# Revit family: Deca_Bacia Carrara_P.606_Caixa Acoplada
name_source: partatom
category: Plumbing Fixtures
revit_build: Autodesk Revit Architecture 2012 (Build: 20110916_2132(x64)
units: mm (PartAtom-declared; Revit-internal decimal feet)

## types (3) — shared parameters
Acompanha o Produto = Não Aplicável
Aprovado por = Contino/quattroD
Atendimento ao Cliente = 0800-011-7073
Consumo = 6 LPF
Criador por = Contino/quattroD
Description = Bacia com caixa acoplada
Descrição = Bacia com caixa acoplada
Diâmetro Ponto de Esgoto = 100 mm  [stored 0.328084 ft]
Fabricante = Deca
Linha = Carrara
Louça/Metais = Louça
Manufacturer = Deca
Material = Cerâmica (Vitreous China)
Norma = NBR15097-1 NBR15097-2
Peso Liquido (Kg) = 33.8
Produto = Bacia para caixa acoplada linha Carrara
Raio Ponto de Esgoto = 50 mm  [stored 0.164042 ft]
Segmento = Banheiro Luxo
URL = www.deca.com.br
Variações de COR = P.606.17, P.606.37 , P.606.95
Vendido Separadamente = Anel de vedação (AV.90.01 ), Ligação flexível (4607.C.030 / 4607.C.040 / 4607.C.050), Parafusos de fixação (SP.13.01)
zero-valued in all types: Default Elevation

## per-type parameters (varying)
| type | Assento | Bacia | Caixa | Caixa_Family | Código | Diâmetro Água Fria | Model | Raio Água Fria |
| Dual Flux 3 lpf / 6 lpf - Branco GE17 | Deca GE17 Branco Gelo Poliéster | Deca GE17 Branco Gelo Cerâmica | Deca GE17 Branco Gelo Cerâmica | Deca_Shared_Caixa Acoplada_P.606 : Dual Flux 3 lpf / 6 lpf - Branco GE17 | P.606.17 | 15 mm  [stored 0.0492126 ft] | P.606.17 | 8 mm  [stored 0.0262467 ft] |
| Dual Flux 3 lpf / 6 lpf - Ébano EB95 | Deca EB95 Ébano Poliéster | Deca EB95 Ébano Cerâmica | Deca EB95 Ébano Cerâmica | Deca_Shared_Caixa Acoplada_P.606 : Dual Flux 3 lpf / 6 lpf - Ébano EB95 | P.606.95 | 13 mm | P.606.95 | 6 mm  [stored 0.019685 ft] |
| Dual Flux 3 lpf / 6 lpf - Creme CR37 | Deca CR37 Creme Poliéster | Deca CR37 Creme Cerâmica | Deca CR37 Creme Cerâmica | Deca_Shared_Caixa Acoplada_P.606 : Dual Flux 3 lpf / 6 lpf - Creme CR37 | P.606.37 | 13 mm | P.606.37 | 6 mm  [stored 0.019685 ft] |

note: [stored X ft] marks values corroborated as IEEE doubles in the binary element streams (Revit-internal decimal feet)

## geometry (parser evidence)
native form markers: Blend x12, Sweep x5
no freeform markers — native parametric forms only
